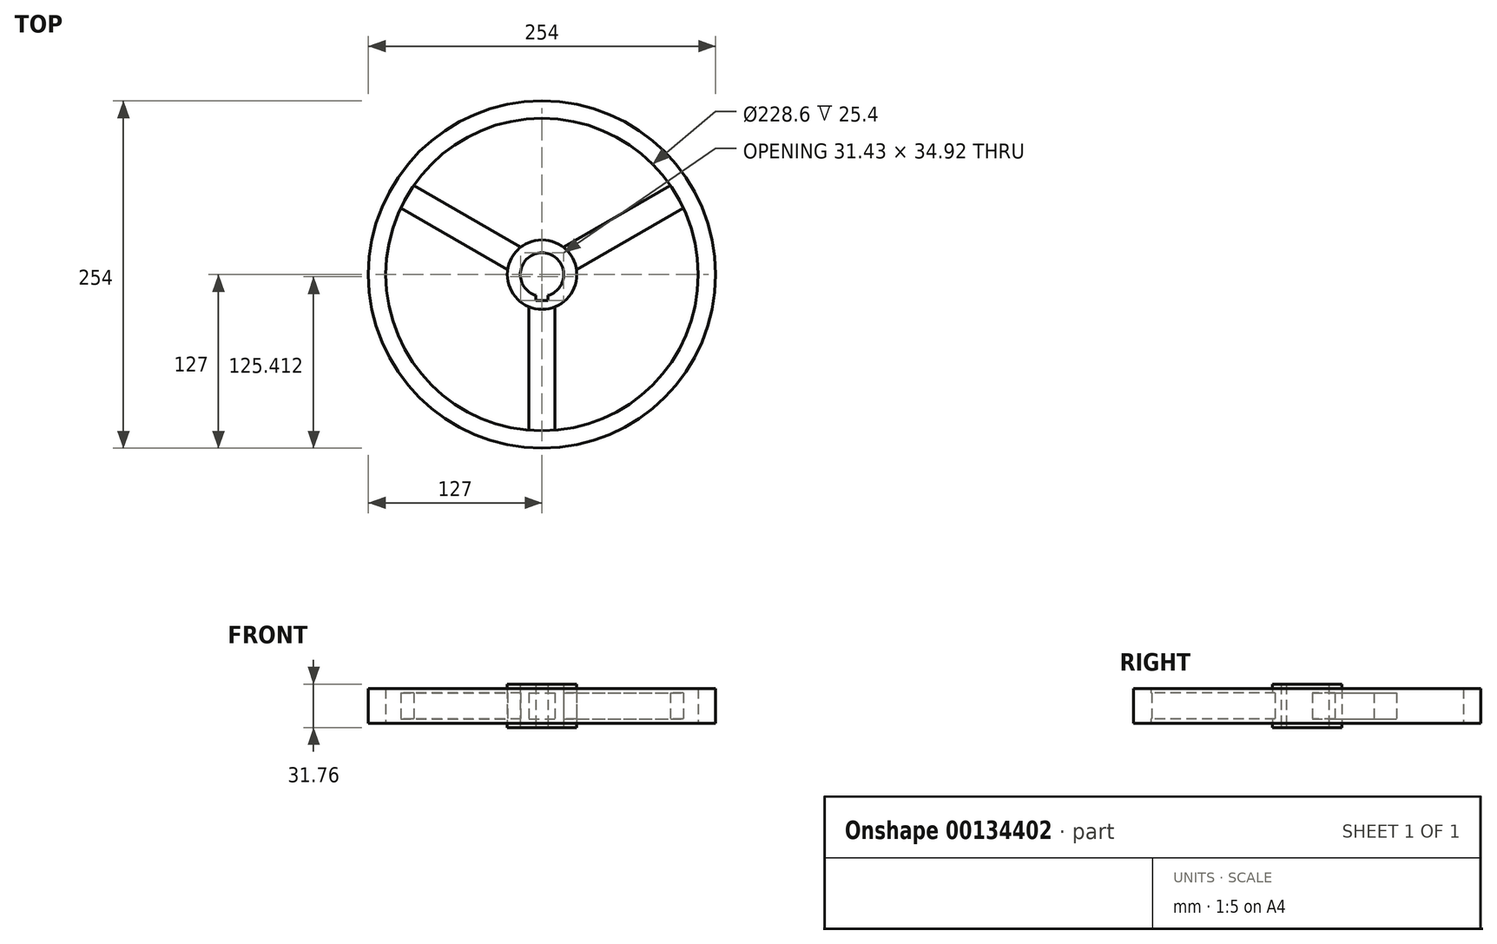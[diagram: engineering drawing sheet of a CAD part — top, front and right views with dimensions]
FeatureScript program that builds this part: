
annotation { "Feature Type Name" : "Feature", "Feature Type Description" : "" }
export const myFeature = defineFeature(function(context is Context, id is Id, definition is map)
    precondition{}
    {
        {
            var Q0;
            Q0=qCreatedBy(makeId("Top.planeOp"),FACE);
            var sketch = newSketch(context, id + "F0", { "sketchPlane" : qUnion([Q0])});
            skCircle(sketch, "E0", {"center": v(0, 0) * mm, "radius": 25.4 * mm});
            skArc(sketch, "E1", {"start": v(4.44, -15.24) * mm, "mid": v(0, 15.88) * mm, "end": v(-4.45, -15.24) * mm});
            skCircle(sketch, "E2", {"center": v(0, 0) * mm, "radius": 114.3 * mm});
            skCircle(sketch, "E3", {"center": v(0, 0) * mm, "radius": 127 * mm});
            skLineSegment(sketch, "E4", {"start": v(0, 0) * mm, "end": v(0, -114.3) * mm, "construction": true});
            skLineSegment(sketch, "E5", {"start": v(9.52, -23.55) * mm, "end": v(9.53, -113.9) * mm});
            skLineSegment(sketch, "E6", {"start": v(-9.53, -23.55) * mm, "end": v(-9.52, -113.9) * mm});
            skLineSegment(sketch, "E7", {"start": v(4.44, 0) * mm, "end": v(4.44, -19.05) * mm, "construction": true});
            skLineSegment(sketch, "E8", {"start": v(4.44, -19.05) * mm, "end": v(-4.45, -19.05) * mm});
            skLineSegment(sketch, "E9", {"start": v(0, 0) * mm, "end": v(4.44, 0) * mm, "construction": true});
            skLineSegment(sketch, "E10", {"start": v(-4.45, -19.05) * mm, "end": v(-4.45, -15.24) * mm});
            skLineSegment(sketch, "E11", {"start": v(4.44, -19.05) * mm, "end": v(4.44, -15.24) * mm});
            skLineSegment(sketch, "E12", {"start": v(0, 0) * mm, "end": v(98.99, 57.15) * mm, "construction": true});
            skLineSegment(sketch, "E13", {"start": v(15.63, 20.02) * mm, "end": v(93.88, 65.2) * mm});
            skLineSegment(sketch, "E14", {"start": v(25.15, 3.52) * mm, "end": v(103.4, 48.7) * mm});
            skLineSegment(sketch, "E15", {"start": v(0, 0) * mm, "end": v(-98.99, 57.15) * mm, "construction": true});
            skLineSegment(sketch, "E16", {"start": v(-15.63, 20.02) * mm, "end": v(-93.88, 65.2) * mm});
            skLineSegment(sketch, "E17", {"start": v(-103.4, 48.7) * mm, "end": v(-25.15, 3.52) * mm});
            skSolve(sketch);
        }
        {
            var Q0;
            Q0=makeQuery(id+"F0.imprint","IMPRINT",FACE,{"disambiguationData":[TD([[makeQuery(id+"F0.imprint","IMPRINT",EDGE,{"derivedFrom":sQuery(id+"F0.wireOp",EDGE,"E1")}),-1.0]])]});
            extrude(context, id + "F1", {"entities" : qUnion([Q0]), "endBound" : BoundingType.SYMMETRIC, "depth" : 31.75 * mm});
        }
        {
            var Q0;
            {var subQ0=sQuery(id+"F0.wireOp",EDGE,"E16");Q0=makeQuery(id+"F0.imprint","IMPRINT",FACE,{"disambiguationData":[TD([[makeQuery(id+"F0.imprint","IMPRINT",EDGE,{"derivedFrom":subQ0}),1.0]])]});}
            var Q1;
            {var subQ0=sQuery(id+"F0.wireOp",EDGE,"E13");Q1=makeQuery(id+"F0.imprint","IMPRINT",FACE,{"disambiguationData":[TD([[makeQuery(id+"F0.imprint","IMPRINT",EDGE,{"derivedFrom":subQ0}),-1.0]])]});}
            var Q2;
            {var subQ0=sQuery(id+"F0.wireOp",EDGE,"E5");Q2=makeQuery(id+"F0.imprint","IMPRINT",FACE,{"disambiguationData":[TD([[makeQuery(id+"F0.imprint","IMPRINT",EDGE,{"derivedFrom":subQ0}),-1.0]])]});}
            extrude(context, id + "F2", {"entities" : qUnion([Q0, Q1, Q2]), "operationType" : NewBodyOperationType.ADD, "endBound" : BoundingType.SYMMETRIC, "depth" : 19.05 * mm});
        }
        {
            var Q0;
            Q0=makeQuery(id+"F0.imprint","IMPRINT",FACE,{"disambiguationData":[TD([[makeQuery(id+"F0.imprint","IMPRINT",EDGE,{"derivedFrom":sQuery(id+"F0.wireOp",EDGE,"E3")}),1.0]])]});
            extrude(context, id + "F3", {"entities" : qUnion([Q0]), "operationType" : NewBodyOperationType.ADD, "endBound" : BoundingType.SYMMETRIC, "depth" : 25.4 * mm});
        }
    });
